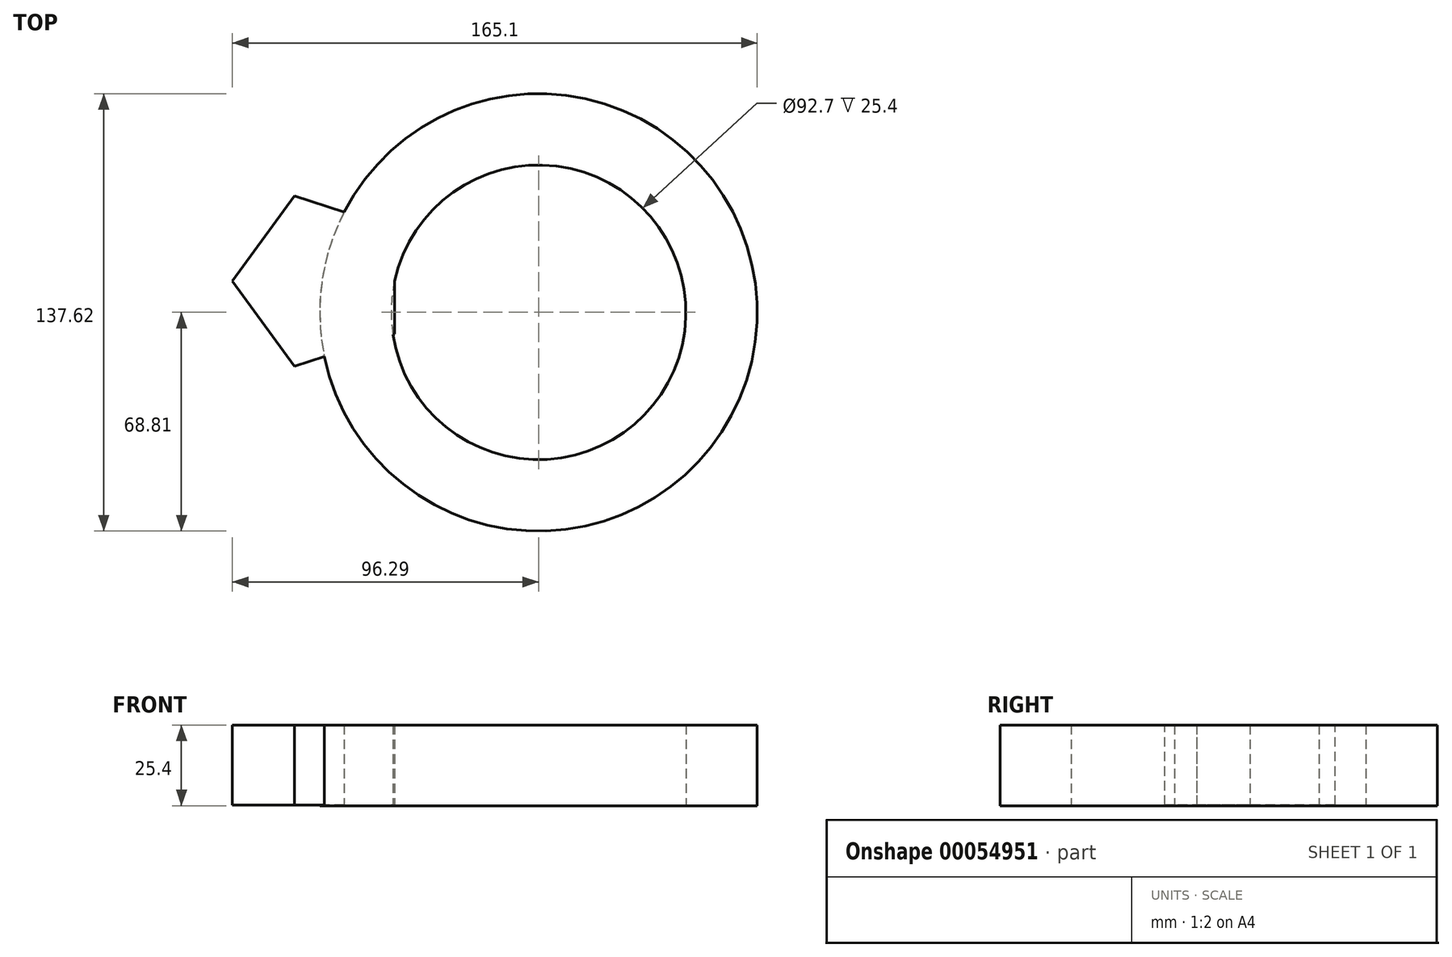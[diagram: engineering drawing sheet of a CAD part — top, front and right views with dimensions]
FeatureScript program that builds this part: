
annotation { "Feature Type Name" : "Feature", "Feature Type Description" : "" }
export const myFeature = defineFeature(function(context is Context, id is Id, definition is map)
    precondition{}
    {
        {
            var Q0;
            Q0=qCreatedBy(makeId("Top.planeOp"),FACE);
            var sketch = newSketch(context, id + "F0", { "sketchPlane" : qUnion([Q0])});
            skCircle(sketch, "E0", {"center": v(0, 0) * mm, "radius": 68.8 * mm});
            skSolve(sketch);
        }
        {
            var Q0;
            Q0=makeQuery(id+"F0.imprint","IMPRINT",FACE,{"disambiguationData":[TD([[makeQuery(id+"F0.imprint","IMPRINT",EDGE,{"derivedFrom":sQuery(id+"F0.wireOp",EDGE,"E0")}),1.0]])]});
            var sketch = newSketch(context, id + "F3", { "sketchPlane" : qUnion([Q0])});
            skCircle(sketch, "E1", {"center": v(0, 0) * mm, "radius": 46.35 * mm});
            skSolve(sketch);
        }
        {
            var Q0;
            Q0=makeQuery(id+"F3.imprint","IMPRINT",FACE,{"disambiguationData":[TD([[makeQuery(id+"F3.imprint","IMPRINT",EDGE,{"derivedFrom":sQuery(id+"F3.wireOp",EDGE,"E1")}),-1.0]])]});
            extrude(context, id + "F1", {"entities" : qUnion([Q0]), "depth" : 25.4 * mm});
        }
        {
            var Q0;
            Q0=makeQuery(id+"F1.opExtrude","CAP_FACE",FACE,{"disambiguationData":[OSD([sQuery(id+"F0.wireOp",EDGE,"E0"),sQuery(id+"F3.wireOp",EDGE,"E1")])],"isStart":false});
            var sketch = newSketch(context, id + "F2", { "sketchPlane" : qUnion([Q0])});
            skCircle(sketch, "E2.cCircle", {"center": v(-68.1, 9.8) * mm, "radius": 22.8 * mm, "construction": true});
            skLineSegment(sketch, "E2.0", {"start": v(-45.3, 26.38) * mm, "end": v(-45.3, -6.76) * mm});
            skLineSegment(sketch, "E2.1", {"start": v(-45.3, -6.76) * mm, "end": v(-76.82, -17) * mm});
            skLineSegment(sketch, "E2.2", {"start": v(-76.82, -17) * mm, "end": v(-96.3, 9.8) * mm});
            skLineSegment(sketch, "E2.3", {"start": v(-96.3, 9.8) * mm, "end": v(-76.82, 36.62) * mm});
            skLineSegment(sketch, "E2.4", {"start": v(-76.82, 36.62) * mm, "end": v(-45.3, 26.38) * mm});
            skPoint(sketch, "E2.0.midPoint", {"position": v(-45.3, 9.8) * mm});
            skSolve(sketch);
        }
        {
            var Q0;
            Q0 = qSketchRegion(id + "F2", true);
            extrude(context, id + "F4", {"entities" : qUnion([Q0]), "operationType" : NewBodyOperationType.ADD, "oppositeDirection" : true, "depth" : 25.2 * mm});
        }
    });
